# Revit family: LAMP_SETI SPOT 900
name_source: partatom
category: Modelos genéricos
revit_build: Autodesk Revit 2018 (Build: 20190510_1515(x64)
units: mm (PartAtom-declared; Revit-internal decimal feet)

## family parameters
Anfitrión = Cara
Compartido = No
Corte con vacíos al cargar = No
Cota de conector redondo = Diámetro de uso
Puede alojar armadura = No
Punto de cálculo de habitación = No
Tipo de pieza = Normal

## types (4) — shared parameters
CRI = 80
Dimensions = 120 x 39 x 900
Elevación por defecto = 1219 mm
Fabricante = LAMP
Gear = Electronic
Initial color = 3000 K
Installation instructions = https://www.lamp.es
Insulation class = II
LED Lifetime = 50000 L90
Lamp = HIGH POWER LED
Last update = 17/02/2022
Luminaire type = Outdoor - Beacon
MacAdam = 3
Manufacturer URL = http://www.lamp.es
Manufacturer country = Spain
Manufacturer name = LAMP
Power Supply = 50Hz 230V
Product URL = https://www.lamp.es
Product datasheet = http://www.lamp.es
Protection rating = IP65 / IK08
Type = HIGH POWER CREE

## per-type parameters (varying)
| type | Descripción | Efficacy | Finish | Initial intensity | Modelo | Photometric web file | Plum | Power | Product code | Weight |
| 80LM 3000 IND ANTHRACITE | SETI SPOT IND 900 WW ANT. | 21 lm/W | Textured anthracite grey | 97 lm | SE1090I05SP830NAB | Cuerpo seti spot 900 : 80LM 3000 IND ANTHRACITE | 5 W | 2 W | SE1090I05SP830NAB | 3.49 kg |
| 107LM 3000 IND BLACK | SETI SPOT IND 900 WW BK. | 28 lm/W | Texturised black | 130 lm | SE1090I05SP830NBW | Cuerpo seti spot 900 : 107LM 3000 IND BLACK | 5 W | 2 W | SE1090I05SP830NBW | 3.49 kg |
| 160LM 3000 DB ANTHRACITE | SETI SPOT DB 900 WW ANT. | 21 lm/W | Textured anthracite grey | 195 lm | SE1090D05SP830NAB | Cuerpo seti spot 900 : 160LM 3000 DB ANTHRACITE | 9 W | 4 W | SE1090D05SP830NAB | 3.72 kg |
| 214LM 3000 DB BLACK | SETI SPOT DB 900 WW BK. | 28 lm/W | Texturised black | 261 lm | SE1090D05SP830NBW | Cuerpo seti spot 900 : 214LM 3000 DB BLACK | 9 W | 4 W | SE1090D05SP830NBW | 3.72 kg |
